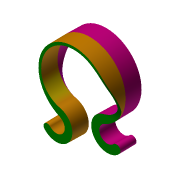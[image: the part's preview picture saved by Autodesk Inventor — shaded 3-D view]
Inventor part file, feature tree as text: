
AUTODESK INVENTOR PART (.ipt)
format: ipt  version: 2014 (Build 180170000, 170)  size: 236,032 bytes
history: native  units: mm
features: extrude x3, sketch x3, fillet x2
ambient origin geometry x8: Origin, YZ Plane, XZ Plane, XY Plane, X Axis, Y Axis, Z Axis, Center Point
bodies: Solid1 (feature_tree)
feature tree (8):
  extrude  "Extrusion1"  Depth=4.3mm
  sketch  "Sketch2"  dims[d12=2.0mm d13=2.0mm]
  sketch  "Sketch3"  dims[d14=15.0deg d15=1.0mm d16=8.0mm d17=-0.174533mm d34=2.0mm d35=2.0mm d36=27.052603mm d38=1.0mm d39=27.052603mm d40=8.0mm d42=0.8mm d44=27.052603mm d45=27.052603mm d49=6.0mm d50=10.0mm d51=0.0mm d52=10.0mm d53=0.0mm d54=10.0mm]
  fillet  "Fillet9"  Radius=4.3mm
  extrude  "Extrusion4"  Depth=2.0mm
  extrude  "Extrusion5"  Depth=10.0mm
  fillet  "Fillet10"  Radius=2.0mm
  sketch  "Sketch1"  dims[d0=0.5mm d1=20.0mm d6=4.3mm d7=4.3mm]
